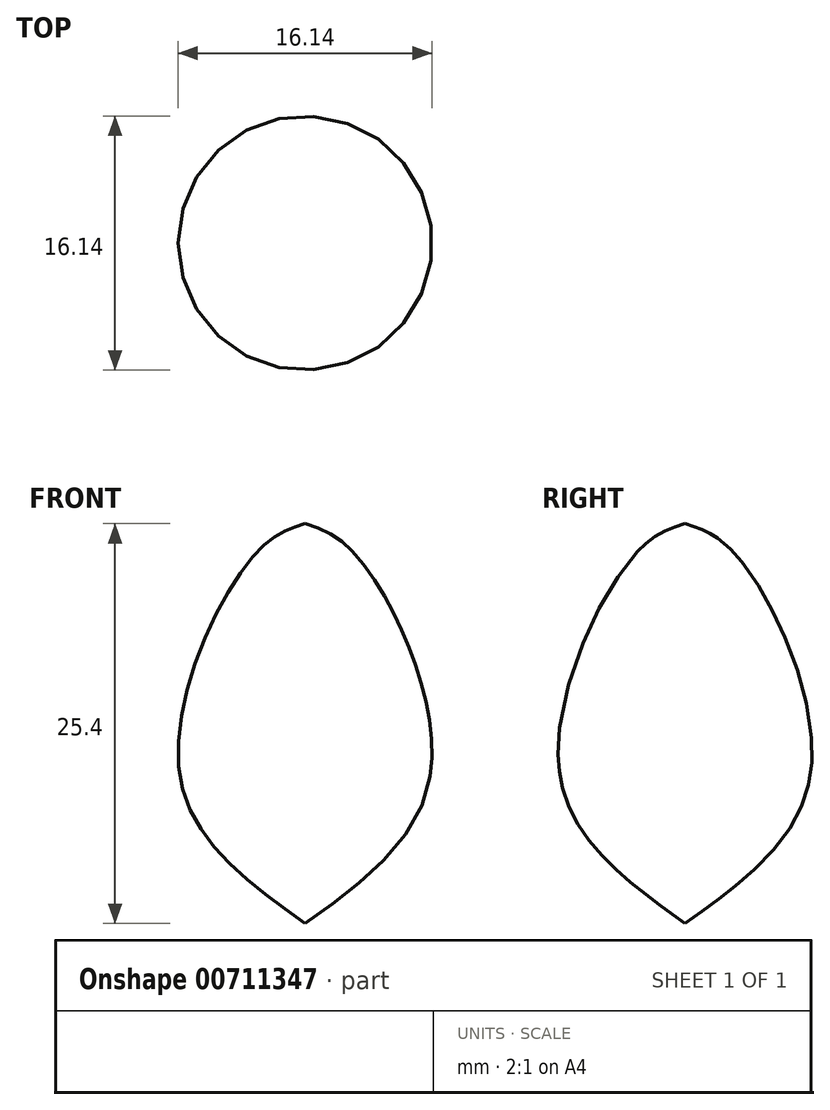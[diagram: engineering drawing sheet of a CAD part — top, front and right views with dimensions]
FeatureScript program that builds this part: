
annotation { "Feature Type Name" : "Feature", "Feature Type Description" : "" }
export const myFeature = defineFeature(function(context is Context, id is Id, definition is map)
    precondition{}
    {
        {
            var Q0;
            Q0=qCreatedBy(makeId("Front.planeOp"),FACE);
            var sketch = newSketch(context, id + "F0", { "sketchPlane" : qUnion([Q0])});
            skLineSegment(sketch, "E0", {"start": v(0, 14.07) * mm, "end": v(0, -11.33) * mm});
            skFitSpline(sketch, "E1", {"points": [v(0, -11.33) * mm, v(-7.99, -1.7) * mm, v(-3.17, 12.13) * mm, v(0, 14.07) * mm], "startDerivative": vector(-29.26, 20.99) * mm, "endDerivative": vector(14.4, 4.5) * mm});
            skSolve(sketch);
        }
        {
            var Q0;
            Q0=makeQuery(id+"F0.imprint","IMPRINT",FACE,{"disambiguationData":[TD([[makeQuery(id+"F0.imprint","IMPRINT",EDGE,{"derivedFrom":sQuery(id+"F0.wireOp",EDGE,"E0")}),-1.0]])]});
            var Q1;
            Q1=sQuery(id+"F0.wireOp",EDGE,"E0");
            revolve(context, id + "F1", {"surfaceOperationType" : NewSurfaceOperationType.NEW, "entities" : qUnion([Q0]), "axis" : qUnion([Q1]), "revolveType" : RevolveType.FULL});
        }
    });
